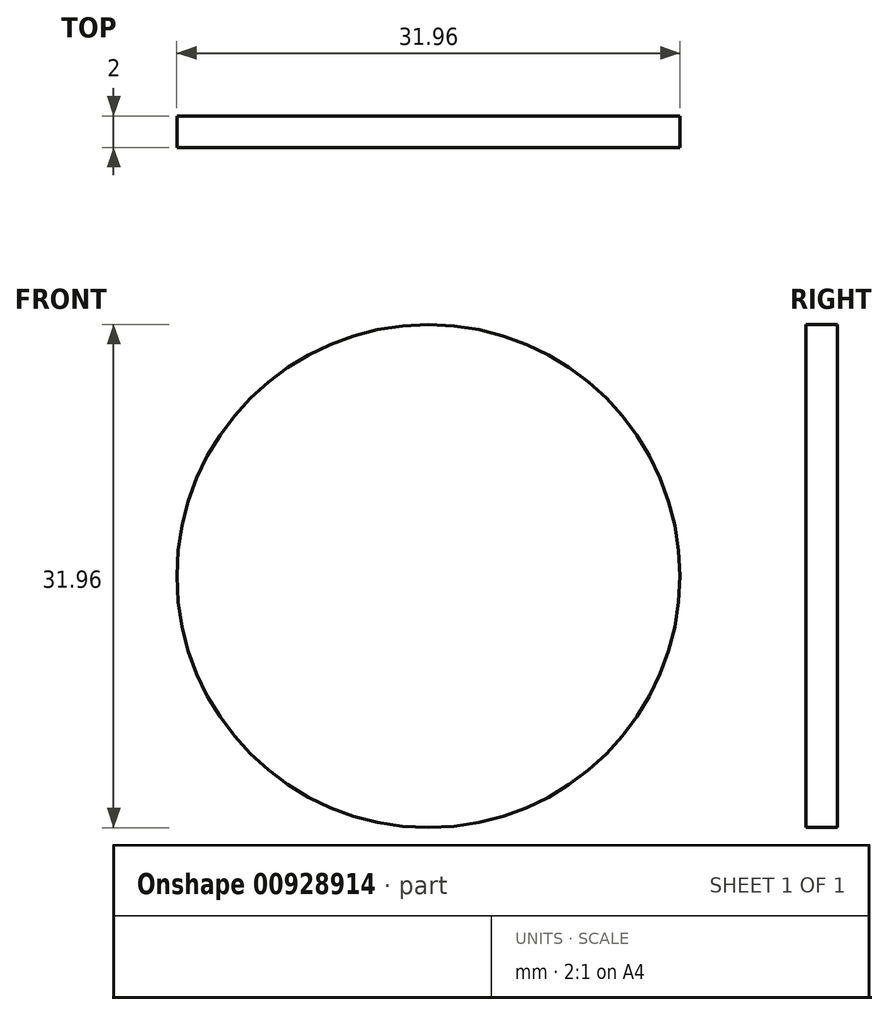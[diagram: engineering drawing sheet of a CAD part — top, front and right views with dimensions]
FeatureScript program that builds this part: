
annotation { "Feature Type Name" : "Feature", "Feature Type Description" : "" }
export const myFeature = defineFeature(function(context is Context, id is Id, definition is map)
    precondition{}
    {
        {
            var Q0;
            Q0=qCreatedBy(makeId("Front.planeOp"),FACE);
            var sketch = newSketch(context, id + "F0", { "sketchPlane" : qUnion([Q0])});
            skCircle(sketch, "E0", {"center": v(0, 0) * mm, "radius": 15.97 * mm});
            skSolve(sketch);
        }
        {
            var Q0;
            Q0=makeQuery(id+"F0.imprint","IMPRINT",FACE,{"disambiguationData":[TD([[makeQuery(id+"F0.imprint","IMPRINT",EDGE,{"derivedFrom":sQuery(id+"F0.wireOp",EDGE,"E0")}),1.0]])]});
            extrude(context, id + "F1", {"entities" : qUnion([Q0]), "depth" : 2 * mm, "offsetDistance" : 25 * mm});
        }
    });
